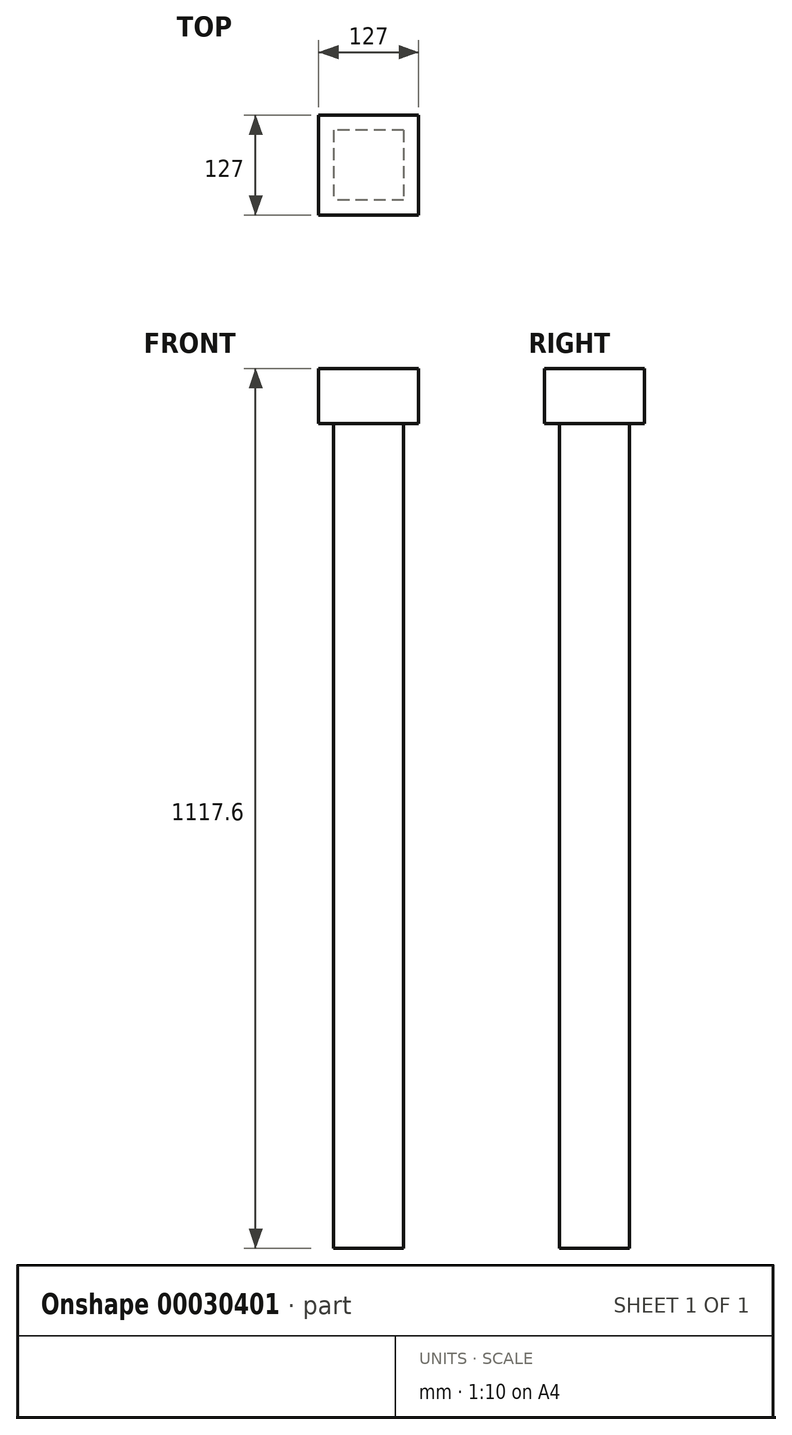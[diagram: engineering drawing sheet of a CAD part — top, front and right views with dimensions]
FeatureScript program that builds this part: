
annotation { "Feature Type Name" : "Feature", "Feature Type Description" : "" }
export const myFeature = defineFeature(function(context is Context, id is Id, definition is map)
    precondition{}
    {
        {
            var Q0;
            Q0=qCreatedBy(makeId("Top.planeOp"),FACE);
            var sketch = newSketch(context, id + "F0", { "sketchPlane" : qUnion([Q0])});
            skLineSegment(sketch, "E0.rect.bottom", {"start": v(44.45, 44.45) * mm, "end": v(-44.45, 44.45) * mm});
            skLineSegment(sketch, "E0.rect.top", {"start": v(44.45, -44.45) * mm, "end": v(-44.45, -44.45) * mm});
            skLineSegment(sketch, "E0.rect.left", {"start": v(44.45, 44.45) * mm, "end": v(44.45, -44.45) * mm});
            skLineSegment(sketch, "E0.rect.right", {"start": v(-44.45, 44.45) * mm, "end": v(-44.45, -44.45) * mm});
            skPoint(sketch, "E0.rect.middle", {"position": v(0, 0) * mm});
            skSolve(sketch);
        }
        {
            var Q0;
            Q0=makeQuery(id+"F0.imprint","IMPRINT",FACE,{"disambiguationData":[TD([[makeQuery(id+"F0.imprint","IMPRINT",EDGE,{"derivedFrom":sQuery(id+"F0.wireOp",EDGE,"E0.rect.bottom")}),1.0]])]});
            extrude(context, id + "F1", {"entities" : qUnion([Q0]), "endBound" : BoundingType.SYMMETRIC, "depth" : 1047.75 * mm});
        }
        {
            var Q0;
            Q0=makeQuery(id+"F1.opExtrude","CAP_FACE",FACE,{"disambiguationData":[OSD([sQuery(id+"F0.wireOp",EDGE,"E0.rect.bottom"),sQuery(id+"F0.wireOp",EDGE,"E0.rect.top"),sQuery(id+"F0.wireOp",EDGE,"E0.rect.left"),sQuery(id+"F0.wireOp",EDGE,"E0.rect.right")])],"isStart":false});
            var sketch = newSketch(context, id + "F2", { "sketchPlane" : qUnion([Q0])});
            skLineSegment(sketch, "E1.rect.bottom", {"start": v(63.5, 63.5) * mm, "end": v(-63.5, 63.5) * mm});
            skLineSegment(sketch, "E1.rect.top", {"start": v(63.5, -63.5) * mm, "end": v(-63.5, -63.5) * mm});
            skLineSegment(sketch, "E1.rect.left", {"start": v(63.5, 63.5) * mm, "end": v(63.5, -63.5) * mm});
            skLineSegment(sketch, "E1.rect.right", {"start": v(-63.5, 63.5) * mm, "end": v(-63.5, -63.5) * mm});
            skPoint(sketch, "E1.rect.middle", {"position": v(0, 0) * mm});
            skSolve(sketch);
        }
        {
            var Q0;
            Q0=makeQuery(id+"F2.imprint","IMPRINT",FACE,{"disambiguationData":[TD([[makeQuery(id+"F2.imprint","IMPRINT",EDGE,{"derivedFrom":sQuery(id+"F2.wireOp",EDGE,"E1.rect.bottom")}),1.0]])]});
            var Q1;
            Q1=makeQuery(id+"F2.imprint","IMPRINT",FACE,{"disambiguationData":[TD([[makeQuery(id+"F2.imprint","IMPRINT",EDGE,{"derivedFrom":makeQuery(id+"F1.opExtrude","CAP_EDGE",EDGE,{"disambiguationData":[OSD([sQuery(id+"F0.wireOp",EDGE,"E0.rect.bottom")])],"isStart":false})}),1.0]])]});
            extrude(context, id + "F3", {"entities" : qUnion([Q0, Q1]), "operationType" : NewBodyOperationType.ADD, "depth" : 69.85 * mm});
        }
    });
